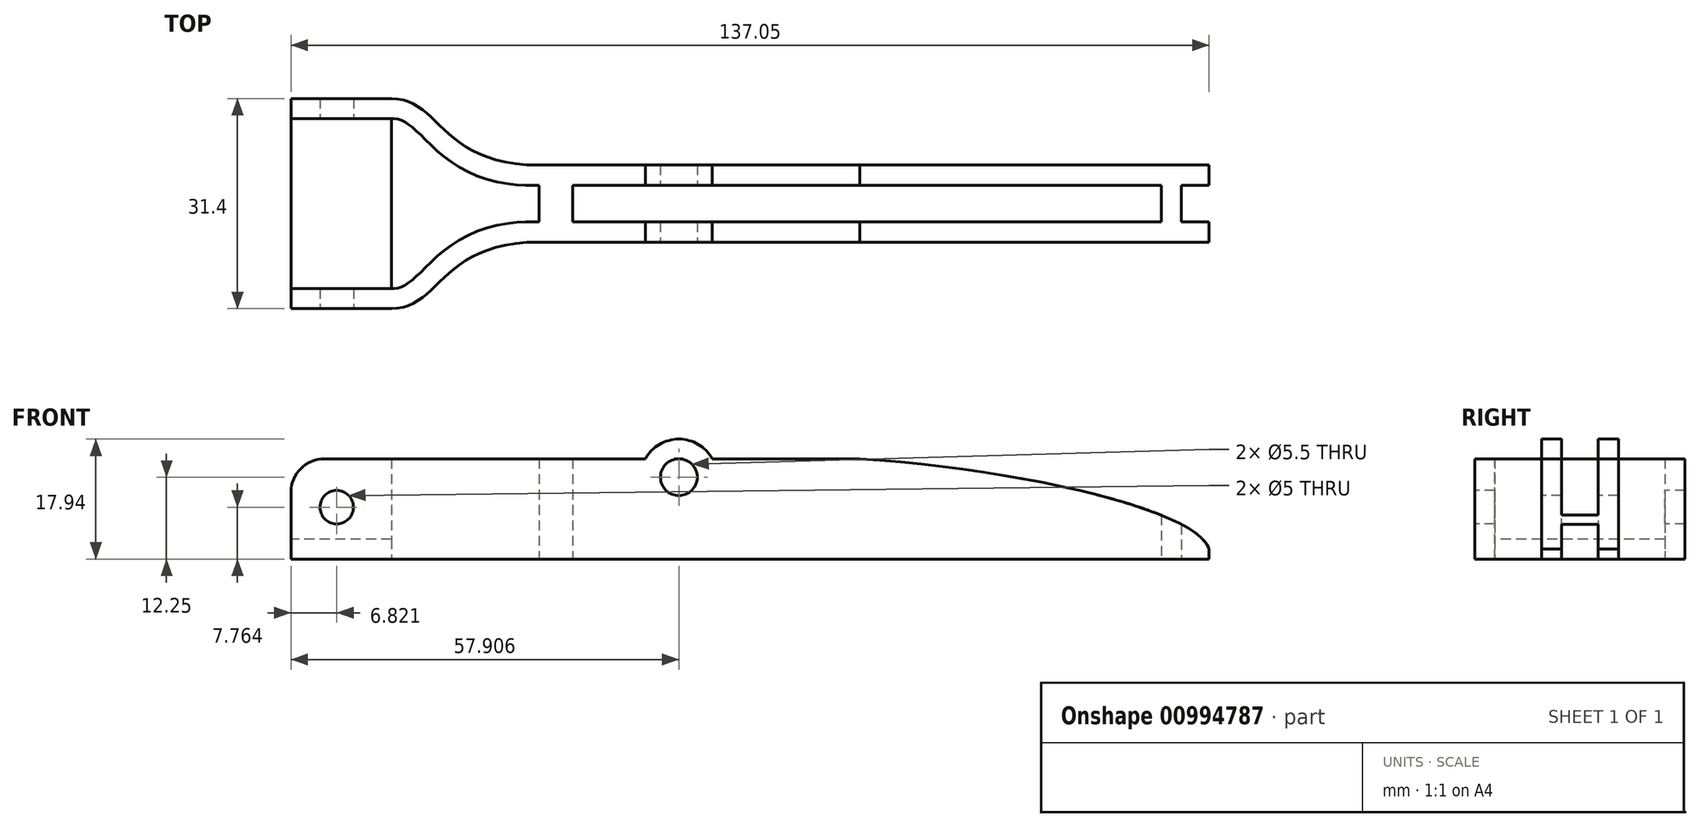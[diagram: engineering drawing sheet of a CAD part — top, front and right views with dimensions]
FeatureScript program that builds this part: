
annotation { "Feature Type Name" : "Feature", "Feature Type Description" : "" }
export const myFeature = defineFeature(function(context is Context, id is Id, definition is map)
    precondition{}
    {
        {
            var Q0;
            Q0=qCreatedBy(makeId("Top.planeOp"),FACE);
            var sketch = newSketch(context, id + "F0", { "sketchPlane" : qUnion([Q0])});
            skLineSegment(sketch, "E0.bottom", {"start": v(-10, 2.75) * mm, "end": v(10, 2.75) * mm});
            skLineSegment(sketch, "E0.top", {"start": v(-10, -2.75) * mm, "end": v(10, -2.75) * mm});
            skLineSegment(sketch, "E0.left", {"start": v(-10, 2.75) * mm, "end": v(-10, -2.75) * mm});
            skLineSegment(sketch, "E0.right", {"start": v(10, 2.75) * mm, "end": v(10, -2.75) * mm});
            skPoint(sketch, "E0.middle", {"position": v(0, 0) * mm});
            skLineSegment(sketch, "E1.bottom", {"start": v(-15, 5.75) * mm, "end": v(15, 5.75) * mm});
            skLineSegment(sketch, "E1.top", {"start": v(-15, -5.75) * mm, "end": v(85, -5.75) * mm});
            skLineSegment(sketch, "E1.left", {"start": v(-15, 5.75) * mm, "end": v(-15, -5.75) * mm});
            skLineSegment(sketch, "E1.right", {"start": v(15, 5.75) * mm, "end": v(15, -5.75) * mm});
            skLineSegment(sketch, "E2", {"start": v(-52.05, -15.7) * mm, "end": v(-37.05, -15.7) * mm});
            skFitSpline(sketch, "E3", {"points": [v(-37.05, -15.7) * mm, v(-15, -5.75) * mm], "startDerivative": vector(21.91, 0) * mm, "endDerivative": vector(44.23, 0) * mm});
            skFitSpline(sketch, "E4.0", {"points": [v(-37.05, -12.7) * mm, v(-36.77, -12.7) * mm, v(-36.27, -12.65) * mm, v(-35.66, -12.48) * mm, v(-35.06, -12.2) * mm, v(-34.4, -11.76) * mm, v(-33.66, -11.16) * mm, v(-32.56, -10.14) * mm, v(-30.93, -8.53) * mm, v(-28.37, -6.4) * mm, v(-24.98, -4.45) * mm, v(-20.62, -3.09) * mm, v(-17.01, -2.75) * mm, v(-15, -2.75) * mm]});
            skLineSegment(sketch, "E5", {"start": v(-37.05, -12.7) * mm, "end": v(-52.05, -12.7) * mm});
            skLineSegment(sketch, "E6", {"start": v(-52.05, -12.7) * mm, "end": v(-52.05, -15.7) * mm});
            skFitSpline(sketch, "E7.MirrorCS", {"points": [v(-37.05, 15.7) * mm, v(-15, 5.75) * mm], "startDerivative": vector(21.91, 0) * mm, "endDerivative": vector(44.23, 0) * mm});
            skLineSegment(sketch, "E8.MirrorCS", {"start": v(-52.05, 15.7) * mm, "end": v(-37.05, 15.7) * mm});
            skLineSegment(sketch, "E9.MirrorCS", {"start": v(-52.05, 12.7) * mm, "end": v(-52.05, 15.7) * mm});
            skLineSegment(sketch, "E10.MirrorCS", {"start": v(-37.05, 12.7) * mm, "end": v(-52.05, 12.7) * mm});
            skFitSpline(sketch, "E11.0", {"points": [v(-37.05, 12.7) * mm, v(-36.77, 12.7) * mm, v(-36.27, 12.65) * mm, v(-35.66, 12.48) * mm, v(-35.06, 12.2) * mm, v(-34.4, 11.76) * mm, v(-33.66, 11.16) * mm, v(-32.56, 10.14) * mm, v(-30.93, 8.53) * mm, v(-28.37, 6.4) * mm, v(-24.98, 4.45) * mm, v(-20.62, 3.09) * mm, v(-17.01, 2.75) * mm, v(-15, 2.75) * mm]});
            skLineSegment(sketch, "E12", {"start": v(-15, -2.75) * mm, "end": v(-10, -2.75) * mm});
            skLineSegment(sketch, "E13", {"start": v(-15, 2.75) * mm, "end": v(-10, 2.75) * mm});
            skLineSegment(sketch, "E14", {"start": v(10, -2.75) * mm, "end": v(15, -2.75) * mm});
            skLineSegment(sketch, "E15", {"start": v(10, 2.75) * mm, "end": v(15, 2.75) * mm});
            skLineSegment(sketch, "E16", {"start": v(15, -2.75) * mm, "end": v(85, -2.75) * mm});
            skLineSegment(sketch, "E17", {"start": v(85, -2.75) * mm, "end": v(85, -5.75) * mm});
            skLineSegment(sketch, "E18.MirrorCS", {"start": v(15, 2.75) * mm, "end": v(85, 2.75) * mm});
            skLineSegment(sketch, "E19.MirrorCS", {"start": v(-15, 5.75) * mm, "end": v(85, 5.75) * mm});
            skLineSegment(sketch, "E20.MirrorCS", {"start": v(85, 2.75) * mm, "end": v(85, 5.75) * mm});
            skLineSegment(sketch, "E21.bottom", {"start": v(41.82, 2.75) * mm, "end": v(44.82, 2.75) * mm});
            skLineSegment(sketch, "E21.top", {"start": v(41.82, -2.75) * mm, "end": v(44.82, -2.75) * mm});
            skLineSegment(sketch, "E21.left", {"start": v(41.82, 2.75) * mm, "end": v(41.82, -2.75) * mm});
            skLineSegment(sketch, "E21.right", {"start": v(44.82, 2.75) * mm, "end": v(44.82, -2.75) * mm});
            skLineSegment(sketch, "E22", {"start": v(-52.05, 12.7) * mm, "end": v(-52.05, -12.7) * mm});
            skLineSegment(sketch, "E23", {"start": v(-37.05, -12.7) * mm, "end": v(-37.05, 12.7) * mm});
            skLineSegment(sketch, "E24", {"start": v(80.87, 2.75) * mm, "end": v(80.87, -2.75) * mm});
            skLineSegment(sketch, "E25", {"start": v(77.87, -2.75) * mm, "end": v(77.87, 2.75) * mm});
            skSolve(sketch);
        }
        {
            var Q0;
            {var subQ0=sQuery(id+"F0.wireOp",EDGE,"E7.MirrorCS");Q0=makeQuery(id+"F0.imprint","IMPRINT",FACE,{"disambiguationData":[TD([[makeQuery(id+"F0.imprint","IMPRINT",EDGE,{"derivedFrom":subQ0}),-1.0]])]});}
            var Q1;
            Q1=makeQuery(id+"F0.imprint","IMPRINT",FACE,{"disambiguationData":[TD([[makeQuery(id+"F0.imprint","IMPRINT",EDGE,{"derivedFrom":sQuery(id+"F0.wireOp",EDGE,"E2")}),1.0]])]});
            var Q2;
            Q2=makeQuery(id+"F0.imprint","IMPRINT",FACE,{"disambiguationData":[TD([[makeQuery(id+"F0.imprint","IMPRINT",EDGE,{"derivedFrom":sQuery(id+"F0.wireOp",EDGE,"E0.top")}),-1.0]])]});
            var Q3;
            Q3=makeQuery(id+"F0.imprint","IMPRINT",FACE,{"disambiguationData":[TD([[makeQuery(id+"F0.imprint","IMPRINT",EDGE,{"derivedFrom":sQuery(id+"F0.wireOp",EDGE,"E0.bottom")}),1.0]])]});
            var Q4;
            {var subQ3=sQuery(id+"F0.wireOp",EDGE,"E20.MirrorCS");Q4=makeQuery(id+"F0.imprint","IMPRINT",FACE,{"disambiguationData":[TD([[makeQuery(id+"F0.imprint","IMPRINT",EDGE,{"derivedFrom":subQ3}),1.0]])]});}
            var Q5;
            {var subQ0=sQuery(id+"F0.wireOp",EDGE,"E17");Q5=makeQuery(id+"F0.imprint","IMPRINT",FACE,{"disambiguationData":[TD([[makeQuery(id+"F0.imprint","IMPRINT",EDGE,{"derivedFrom":subQ0}),-1.0]])]});}
            var Q6;
            Q6=makeQuery(id+"F0.imprint","IMPRINT",FACE,{"disambiguationData":[TD([[makeQuery(id+"F0.imprint","IMPRINT",EDGE,{"derivedFrom":sQuery(id+"F0.wireOp",EDGE,"E0.left")}),-1.0]])]});
            var Q7;
            Q7=makeQuery(id+"F0.imprint","IMPRINT",FACE,{"disambiguationData":[TD([[makeQuery(id+"F0.imprint","IMPRINT",EDGE,{"derivedFrom":sQuery(id+"F0.wireOp",EDGE,"E21.bottom")}),-1.0]])]});
            var Q8;
            {var subQ7=sQuery(id+"F0.wireOp",EDGE,"E21.bottom");Q8=makeQuery(id+"F0.imprint","IMPRINT",FACE,{"disambiguationData":[TD([[makeQuery(id+"F0.imprint","IMPRINT",EDGE,{"derivedFrom":subQ7}),1.0]])]});}
            var Q9;
            {var subQ3=sQuery(id+"F0.wireOp",EDGE,"E21.top");Q9=makeQuery(id+"F0.imprint","IMPRINT",FACE,{"disambiguationData":[TD([[makeQuery(id+"F0.imprint","IMPRINT",EDGE,{"derivedFrom":subQ3}),-1.0]])]});}
            var Q10;
            Q10=makeQuery(id+"F0.imprint","IMPRINT",FACE,{"disambiguationData":[TD([[makeQuery(id+"F0.imprint","IMPRINT",EDGE,{"derivedFrom":sQuery(id+"F0.wireOp",EDGE,"9dc6e1e1-b902-440d-89f8-d2d5fe0496a3")}),1.0]])]});
            var Q11;
            Q11=makeQuery(id+"F0.imprint","IMPRINT",FACE,{"disambiguationData":[TD([[makeQuery(id+"F0.imprint","IMPRINT",EDGE,{"derivedFrom":sQuery(id+"F0.wireOp",EDGE,"4b5528ab-3784-458f-b2e2-aaaa297660d40.MirrorCS")}),-1.0]])]});
            extrude(context, id + "F1", {"entities" : qUnion([Q0, Q1, Q2, Q3, Q4, Q5, Q6, Q7, Q8, Q9, Q10, Q11]), "depth" : 15 * mm, "offsetDistance" : 25 * mm});
        }
        {
            var Q0;
            Q0=makeQuery(id+"F1.opExtrude","SWEPT_FACE",FACE,{"disambiguationData":[OSD([sQuery(id+"F0.wireOp",EDGE,"E2")])]});
            var sketch = newSketch(context, id + "F2", { "sketchPlane" : qUnion([Q0])});
            skCircle(sketch, "E26", {"center": v(-45.23, 7.76) * mm, "radius": 2.5 * mm});
            skCircle(sketch, "E27", {"center": v(5.86, 12.25) * mm, "radius": 2.75 * mm});
            skLineSegment(sketch, "E28.0.2", {"start": v(90.93, 15) * mm, "end": v(-15, 15) * mm});
            skLineSegment(sketch, "E28.0.3", {"start": v(-15, 15) * mm, "end": v(-15, 0) * mm});
            skLineSegment(sketch, "E28.0.4", {"start": v(-15, 0) * mm, "end": v(85, 0) * mm});
            skLineSegment(sketch, "E28.0.5", {"start": v(85, 0) * mm, "end": v(85, 3) * mm});
            skArc(sketch, "E29", {"start": v(10.84, 15) * mm, "mid": v(5.86, 17.94) * mm, "end": v(0.87, 15) * mm});
            skPoint(sketch, "E30", {"position": v(-15, 7.5) * mm});
            skFitSpline(sketch, "E31", {"points": [v(32.88, 15) * mm, v(85, 1.5) * mm], "startDerivative": vector(69.42, -4.32) * mm, "endDerivative": vector(5.16, -17.93) * mm});
            skLineSegment(sketch, "E32", {"start": v(32.88, 15) * mm, "end": v(32.88, 18.45) * mm});
            skLineSegment(sketch, "E33", {"start": v(32.88, 18.45) * mm, "end": v(92.76, 18.45) * mm});
            skLineSegment(sketch, "E34", {"start": v(92.76, 18.45) * mm, "end": v(92.76, 1.5) * mm});
            skLineSegment(sketch, "E35", {"start": v(92.76, 1.5) * mm, "end": v(85, 1.5) * mm});
            skSolve(sketch);
        }
        {
            var Q0;
            {var subQ0=sQuery(id+"F2.wireOp",EDGE,"E29");Q0=makeQuery(id+"F2.imprint","IMPRINT",FACE,{"disambiguationData":[TD([[makeQuery(id+"F2.imprint","IMPRINT",EDGE,{"derivedFrom":subQ0}),1.0]])]});}
            extrude(context, id + "F3", {"entities" : qUnion([Q0]), "operationType" : NewBodyOperationType.ADD, "oppositeDirection" : true, "depth" : (9.95 + 3 + 5.5 + 3) * mm, "offsetDistance" : 25 * mm});
        }
        {
            var Q0;
            Q0=makeQuery(id+"F3.opExtrude","CAP_FACE",FACE,{"disambiguationData":[OSD([sQuery(id+"F2.wireOp",EDGE,"E28.0.2"),sQuery(id+"F2.wireOp",EDGE,"E29")])],"isStart":true});
            extrude(context, id + "F4", {"entities" : qUnion([Q0]), "operationType" : NewBodyOperationType.REMOVE, "oppositeDirection" : true, "depth" : 9.95 * mm, "offsetDistance" : 25 * mm});
        }
        {
            var Q0;
            Q0=makeQuery(id+"F0.imprint","IMPRINT",FACE,{"disambiguationData":[TD([[makeQuery(id+"F0.imprint","IMPRINT",EDGE,{"derivedFrom":sQuery(id+"F0.wireOp",EDGE,"E0.bottom")}),-1.0]])]});
            var Q1;
            {var subQ5=sQuery(id+"F0.wireOp",EDGE,"E21.left");Q1=makeQuery(id+"F0.imprint","IMPRINT",FACE,{"disambiguationData":[TD([[makeQuery(id+"F0.imprint","IMPRINT",EDGE,{"derivedFrom":subQ5}),-1.0]])]});}
            var Q2;
            Q2=makeQuery(id+"F0.imprint","IMPRINT",FACE,{"disambiguationData":[TD([[makeQuery(id+"F0.imprint","IMPRINT",EDGE,{"derivedFrom":sQuery(id+"F0.wireOp",EDGE,"E0.right")}),1.0]])]});
            extrude(context, id + "F5", {"entities" : qUnion([Q0, Q1, Q2]), "operationType" : NewBodyOperationType.REMOVE, "depth" : 55 * mm, "offsetDistance" : 25 * mm});
        }
        {
            var Q0;
            Q0=makeQuery(id+"F2.imprint","IMPRINT",FACE,{"disambiguationData":[TD([[makeQuery(id+"F2.imprint","IMPRINT",EDGE,{"derivedFrom":sQuery(id+"F2.wireOp",EDGE,"E27")}),1.0]])]});
            extrude(context, id + "F6", {"entities" : qUnion([Q0]), "operationType" : NewBodyOperationType.REMOVE, "oppositeDirection" : true, "depth" : 55 * mm, "offsetDistance" : 25 * mm});
        }
        {
            var Q0;
            Q0=makeQuery(id+"F2.imprint","IMPRINT",FACE,{"disambiguationData":[TD([[makeQuery(id+"F2.imprint","IMPRINT",EDGE,{"derivedFrom":sQuery(id+"F2.wireOp",EDGE,"E26")}),1.0]])]});
            extrude(context, id + "F7", {"entities" : qUnion([Q0]), "operationType" : NewBodyOperationType.REMOVE, "oppositeDirection" : true, "depth" : 77 * mm, "offsetDistance" : 25 * mm});
        }
        {
            var Q0;
            Q0=makeQuery(id+"F1.opExtrude","CAP_EDGE",EDGE,{"disambiguationData":[OSD([sQuery(id+"F0.wireOp",EDGE,"E9.MirrorCS")])],"isStart":false});
            var Q1;
            Q1=makeQuery(id+"F1.opExtrude","CAP_EDGE",EDGE,{"disambiguationData":[OSD([sQuery(id+"F0.wireOp",EDGE,"E6")])],"isStart":false});
            fillet(context, id + "F8", {"entities" : qUnion([Q0, Q1]), "radius" : 5 * mm, "tangentPropagation" : true, "allowEdgeOverflow" : false});
        }
        {
            var Q0;
            {var subQ0=sQuery(id+"F0.wireOp",EDGE,"E24");Q0=makeQuery(id+"F0.imprint","IMPRINT",FACE,{"disambiguationData":[TD([[makeQuery(id+"F0.imprint","IMPRINT",EDGE,{"derivedFrom":subQ0}),-1.0]])]});}
            extrude(context, id + "F9", {"entities" : qUnion([Q0]), "operationType" : NewBodyOperationType.ADD, "depth" : 15 * mm, "offsetDistance" : 25 * mm});
        }
        {
            var Q0;
            {var subQ0=sQuery(id+"F0.wireOp",EDGE,"E22");Q0=makeQuery(id+"F0.imprint","IMPRINT",FACE,{"disambiguationData":[TD([[makeQuery(id+"F0.imprint","IMPRINT",EDGE,{"derivedFrom":subQ0}),1.0]])]});}
            extrude(context, id + "F10", {"entities" : qUnion([Q0]), "operationType" : NewBodyOperationType.ADD, "depth" : 3 * mm, "offsetDistance" : 25 * mm});
        }
        {
            var Q0;
            Q0=makeQuery(id+"F2.imprint","IMPRINT",FACE,{"disambiguationData":[TD([[makeQuery(id+"F2.imprint","IMPRINT",EDGE,{"derivedFrom":sQuery(id+"F2.wireOp",EDGE,"E31")}),1.0]])]});
            extrude(context, id + "F11", {"entities" : qUnion([Q0]), "operationType" : NewBodyOperationType.REMOVE, "oppositeDirection" : true, "depth" : 25 * mm, "offsetDistance" : 25 * mm});
        }
    });
